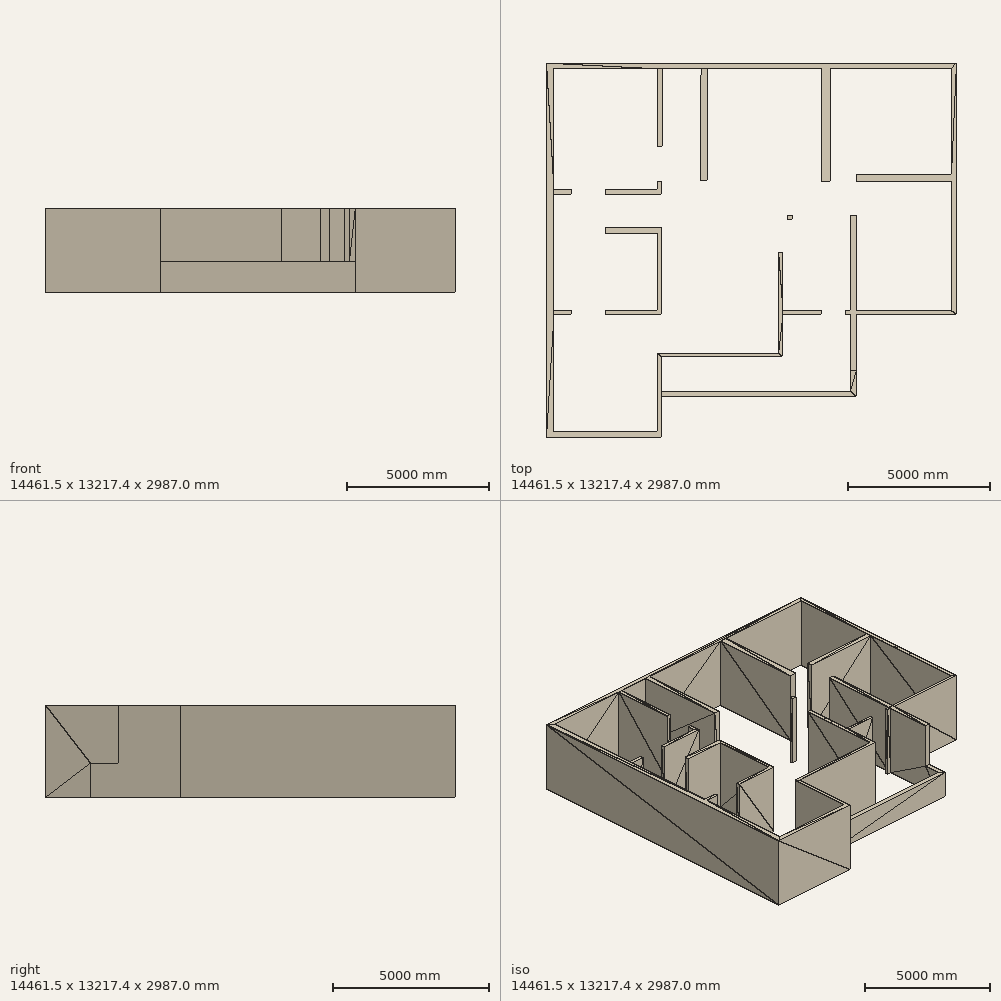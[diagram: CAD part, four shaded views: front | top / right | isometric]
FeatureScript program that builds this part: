
annotation { "Feature Type Name" : "Feature", "Feature Type Description" : "" }
export const myFeature = defineFeature(function(context is Context, id is Id, definition is map)
    precondition{}
    {
        {
            var Q0;
            Q0=qCreatedBy(makeId("Top.planeOp"),FACE);
            var sketch = newSketch(context, id + "F0", { "sketchPlane" : qUnion([Q0])});
            skLineSegment(sketch, "E0", {"start": v(0, 0) * mm, "end": v(-279.4, 0) * mm});
            skLineSegment(sketch, "E1", {"start": v(-863.6, -355.6) * mm, "end": v(-1168.4, -355.6) * mm});
            skLineSegment(sketch, "E2", {"start": v(-1168.4, -355.6) * mm, "end": v(-1168.4, -12.28) * mm});
            skLineSegment(sketch, "E3", {"start": v(-297.04, 0) * mm, "end": v(-311.21, 0) * mm});
            skLineSegment(sketch, "E4", {"start": v(0, 0) * mm, "end": v(0, 381) * mm});
            skLineSegment(sketch, "E5", {"start": v(-279.4, 381) * mm, "end": v(0, 381) * mm});
            skLineSegment(sketch, "E6", {"start": v(0, 399.22) * mm, "end": v(0, 711.2) * mm});
            skLineSegment(sketch, "E7", {"start": v(0, 711.2) * mm, "end": v(-355.6, 711.2) * mm});
            skLineSegment(sketch, "E8.bottom", {"start": v(-482.6, 279.4) * mm, "end": v(-467.2, 279.4) * mm});
            skLineSegment(sketch, "E8.top", {"start": v(-482.6, 268.26) * mm, "end": v(-467.2, 268.26) * mm});
            skLineSegment(sketch, "E8.left", {"start": v(-482.6, 279.4) * mm, "end": v(-482.6, 268.26) * mm});
            skLineSegment(sketch, "E8.right", {"start": v(-467.2, 279.4) * mm, "end": v(-467.2, 268.26) * mm});
            skLineSegment(sketch, "E9", {"start": v(-508, 0) * mm, "end": v(-508, -124.73) * mm});
            skLineSegment(sketch, "E10", {"start": v(-508, -124.73) * mm, "end": v(-863.6, -124.73) * mm});
            skLineSegment(sketch, "E11", {"start": v(-355.6, 381.3) * mm, "end": v(-355.6, 711.2) * mm});
            skLineSegment(sketch, "E12", {"start": v(-1168.4, 711.2) * mm, "end": v(-1168.4, 355.6) * mm});
            skLineSegment(sketch, "E13", {"start": v(-1168.4, 342.47) * mm, "end": v(-1168.4, 0) * mm});
            skLineSegment(sketch, "E14", {"start": v(-1168.4, 355.6) * mm, "end": v(-1117.6, 355.6) * mm});
            skLineSegment(sketch, "E15", {"start": v(-863.6, 355.6) * mm, "end": v(-863.6, 381) * mm});
            skLineSegment(sketch, "E16", {"start": v(-737.43, 382.75) * mm, "end": v(-736.18, 711.2) * mm});
            skLineSegment(sketch, "E17", {"start": v(-863.6, 711.2) * mm, "end": v(-863.6, 482.6) * mm});
            skLineSegment(sketch, "E18", {"start": v(-863.6, 0) * mm, "end": v(-863.6, 228.6) * mm});
            skLineSegment(sketch, "E19", {"start": v(-279.4, 0) * mm, "end": v(-279.4, 279.4) * mm});
            skLineSegment(sketch, "E20", {"start": v(-863.6, -355.6) * mm, "end": v(-863.6, -124.73) * mm});
            skLineSegment(sketch, "E21", {"start": v(-863.6, 0) * mm, "end": v(-1016, 0) * mm});
            skLineSegment(sketch, "E22", {"start": v(-1168.4, 0) * mm, "end": v(-1117.6, 0) * mm});
            skLineSegment(sketch, "E23", {"start": v(-863.6, 228.6) * mm, "end": v(-1016, 228.6) * mm});
            skLineSegment(sketch, "E24", {"start": v(-737.43, 382.75) * mm, "end": v(-716.3, 382.67) * mm});
            skLineSegment(sketch, "E25", {"start": v(-716.3, 382.67) * mm, "end": v(-716.3, 711.2) * mm});
            skLineSegment(sketch, "E26.trimOffspring", {"start": v(-736.18, 711.2) * mm, "end": v(-849.36, 711.2) * mm});
            skLineSegment(sketch, "E27", {"start": v(-849.36, 711.2) * mm, "end": v(-849.36, 482.6) * mm});
            skLineSegment(sketch, "E28", {"start": v(-849.36, 482.6) * mm, "end": v(-863.6, 482.6) * mm});
            skLineSegment(sketch, "E29.trimOffspring", {"start": v(-863.6, 711.2) * mm, "end": v(-1168.4, 711.2) * mm});
            skLineSegment(sketch, "E30", {"start": v(-1168.4, 342.47) * mm, "end": v(-1117.6, 342.47) * mm});
            skLineSegment(sketch, "E31", {"start": v(-852.49, 342.47) * mm, "end": v(-852.49, 381) * mm});
            skLineSegment(sketch, "E32", {"start": v(-852.49, 381) * mm, "end": v(-863.6, 381) * mm});
            skLineSegment(sketch, "E33", {"start": v(-1016, 228.6) * mm, "end": v(-1016, 244.83) * mm});
            skLineSegment(sketch, "E34", {"start": v(-1016, 244.83) * mm, "end": v(-852.49, 244.83) * mm});
            skLineSegment(sketch, "E35", {"start": v(-852.49, 244.83) * mm, "end": v(-852.49, -12.28) * mm});
            skLineSegment(sketch, "E36", {"start": v(-852.49, -12.28) * mm, "end": v(-1016, -12.28) * mm});
            skLineSegment(sketch, "E37", {"start": v(-1016, -12.28) * mm, "end": v(-1016, 0) * mm});
            skLineSegment(sketch, "E38", {"start": v(-1117.6, 0) * mm, "end": v(-1117.6, -12.28) * mm});
            skLineSegment(sketch, "E39", {"start": v(-1117.6, -12.28) * mm, "end": v(-1168.4, -12.28) * mm});
            skLineSegment(sketch, "E40", {"start": v(-279.4, 279.4) * mm, "end": v(-297.04, 279.4) * mm});
            skLineSegment(sketch, "E41", {"start": v(-297.04, 279.4) * mm, "end": v(-297.04, 0) * mm});
            skLineSegment(sketch, "E42", {"start": v(-279.4, 381) * mm, "end": v(-279.4, 399.44) * mm});
            skLineSegment(sketch, "E43", {"start": v(-279.4, 399.44) * mm, "end": v(0, 399.22) * mm});
            skLineSegment(sketch, "E44", {"start": v(-355.6, 381.3) * mm, "end": v(-380.93, 381.31) * mm});
            skLineSegment(sketch, "E45", {"start": v(-380.93, 381.31) * mm, "end": v(-380.93, 711.2) * mm});
            skLineSegment(sketch, "E46.trimOffspring", {"start": v(-380.93, 711.2) * mm, "end": v(-716.3, 711.2) * mm});
            skLineSegment(sketch, "E47", {"start": v(-1190.38, -355.6) * mm, "end": v(-1190.38, 727.92) * mm});
            skLineSegment(sketch, "E48", {"start": v(-1190.38, 727.92) * mm, "end": v(14.74, 727.92) * mm});
            skLineSegment(sketch, "E49", {"start": v(14.74, 727.92) * mm, "end": v(14.74, -10.6) * mm});
            skLineSegment(sketch, "E50", {"start": v(14.74, -10.6) * mm, "end": v(-279.4, -10.6) * mm});
            skLineSegment(sketch, "E51", {"start": v(-495.3, -10.6) * mm, "end": v(-495.3, -135.14) * mm});
            skLineSegment(sketch, "E52", {"start": v(-495.3, -135.14) * mm, "end": v(-852.25, -135.14) * mm});
            skLineSegment(sketch, "E53", {"start": v(-852.25, -135.14) * mm, "end": v(-852.25, -237.06) * mm});
            skLineSegment(sketch, "E54", {"start": v(-852.25, -373.53) * mm, "end": v(-1190.38, -373.53) * mm});
            skLineSegment(sketch, "E55", {"start": v(-1190.38, -373.53) * mm, "end": v(-1190.38, -355.6) * mm});
            skLineSegment(sketch, "E56", {"start": v(-311.21, 0) * mm, "end": v(-311.21, -10.6) * mm});
            skLineSegment(sketch, "E57", {"start": v(-382.22, 0) * mm, "end": v(-382.22, -10.6) * mm});
            skLineSegment(sketch, "E58.trimOffspring", {"start": v(-382.22, 0) * mm, "end": v(-495.3, 0) * mm});
            skLineSegment(sketch, "E59.trimOffspring", {"start": v(-382.22, -10.6) * mm, "end": v(-495.3, -10.6) * mm});
            skLineSegment(sketch, "E60", {"start": v(-279.4, -10.6) * mm, "end": v(-279.4, -252.35) * mm});
            skLineSegment(sketch, "E61", {"start": v(-279.4, -252.35) * mm, "end": v(-852.25, -252.35) * mm});
            skLineSegment(sketch, "E62", {"start": v(-297.04, -10.6) * mm, "end": v(-297.04, -237.06) * mm});
            skLineSegment(sketch, "E63", {"start": v(-297.04, -237.06) * mm, "end": v(-852.25, -237.06) * mm});
            skLineSegment(sketch, "E64.trimOffspring", {"start": v(-852.25, -252.35) * mm, "end": v(-852.25, -373.53) * mm});
            skLineSegment(sketch, "E65.trimOffspring", {"start": v(-297.04, -10.6) * mm, "end": v(-311.21, -10.6) * mm});
            skLineSegment(sketch, "E66", {"start": v(-1117.6, 342.47) * mm, "end": v(-1117.6, 355.6) * mm});
            skLineSegment(sketch, "E67", {"start": v(-1016, 342.47) * mm, "end": v(-1016, 355.6) * mm});
            skLineSegment(sketch, "E68.trimOffspring", {"start": v(-1016, 355.6) * mm, "end": v(-863.6, 355.6) * mm});
            skLineSegment(sketch, "E69.trimOffspring", {"start": v(-1016, 342.47) * mm, "end": v(-852.49, 342.47) * mm});
            skLineSegment(sketch, "E70", {"start": v(-508, 0) * mm, "end": v(-508, 170.24) * mm});
            skLineSegment(sketch, "E71", {"start": v(-508, 170.24) * mm, "end": v(-495.3, 170.24) * mm});
            skLineSegment(sketch, "E72", {"start": v(-495.3, 170.24) * mm, "end": v(-495.3, 0) * mm});
            skSolve(sketch);
        }
        {
            var Q0;
            Q0=makeQuery(id+"F0.imprint","IMPRINT",FACE,{"disambiguationData":[TD([[makeQuery(id+"F0.imprint","IMPRINT",EDGE,{"derivedFrom":sQuery(id+"F0.wireOp",EDGE,"E0")}),1.0]])]});
            var Q1;
            Q1=makeQuery(id+"F0.imprint","IMPRINT",FACE,{"disambiguationData":[TD([[makeQuery(id+"F0.imprint","IMPRINT",EDGE,{"derivedFrom":sQuery(id+"F0.wireOp",EDGE,"E18")}),-1.0]])]});
            var Q2;
            Q2=makeQuery(id+"F0.imprint","IMPRINT",FACE,{"disambiguationData":[TD([[makeQuery(id+"F0.imprint","IMPRINT",EDGE,{"derivedFrom":sQuery(id+"F0.wireOp",EDGE,"E8.bottom")}),-1.0]])]});
            var Q3;
            Q3=makeQuery(id+"F0.imprint","IMPRINT",FACE,{"disambiguationData":[TD([[makeQuery(id+"F0.imprint","IMPRINT",EDGE,{"derivedFrom":sQuery(id+"F0.wireOp",EDGE,"E15")}),-1.0]])]});
            extrude(context, id + "F1", {"entities" : qUnion([Q0, Q1, Q2, Q3]), "depth" : 248.92 * mm});
        }
        {
            var Q0;
            Q0=makeQuery(id+"F1.opExtrude","SWEPT_FACE",FACE,{"disambiguationData":[OSD([sQuery(id+"F0.wireOp",EDGE,"E61")])]});
            var sketch = newSketch(context, id + "F2", { "sketchPlane" : qUnion([Q0])});
            skLineSegment(sketch, "E73.bottom", {"start": v(-852.25, 248.92) * mm, "end": v(-279.4, 248.92) * mm});
            skLineSegment(sketch, "E73.top", {"start": v(-852.25, 92.8) * mm, "end": v(-279.4, 92.8) * mm});
            skLineSegment(sketch, "E73.left", {"start": v(-852.25, 248.92) * mm, "end": v(-852.25, 92.8) * mm});
            skLineSegment(sketch, "E73.right", {"start": v(-279.4, 248.92) * mm, "end": v(-279.4, 92.8) * mm});
            skSolve(sketch);
        }
        {
            var Q0;
            Q0=makeQuery(id+"F2.imprint","IMPRINT",FACE,{"disambiguationData":[TD([[makeQuery(id+"F2.imprint","IMPRINT",EDGE,{"derivedFrom":sQuery(id+"F2.wireOp",EDGE,"E73.bottom")}),1.0]])]});
            extrude(context, id + "F3", {"entities" : qUnion([Q0]), "operationType" : NewBodyOperationType.REMOVE, "oppositeDirection" : true, "depth" : 76.2 * mm});
        }
        {
            var Q0;
            Q0=makeQuery(id+"F1.opExtrude","SWEPT_BODY",BODY,{"disambiguationData":[OSD([sQuery(id+"F0.wireOp",EDGE,"E0"),sQuery(id+"F0.wireOp",EDGE,"E1"),sQuery(id+"F0.wireOp",EDGE,"E2"),sQuery(id+"F0.wireOp",EDGE,"E3"),sQuery(id+"F0.wireOp",EDGE,"E4"),sQuery(id+"F0.wireOp",EDGE,"E5"),sQuery(id+"F0.wireOp",EDGE,"E6"),sQuery(id+"F0.wireOp",EDGE,"E7"),sQuery(id+"F0.wireOp",EDGE,"E9"),sQuery(id+"F0.wireOp",EDGE,"E10"),sQuery(id+"F0.wireOp",EDGE,"E11"),sQuery(id+"F0.wireOp",EDGE,"E12"),sQuery(id+"F0.wireOp",EDGE,"E13"),sQuery(id+"F0.wireOp",EDGE,"E14"),sQuery(id+"F0.wireOp",EDGE,"E15"),sQuery(id+"F0.wireOp",EDGE,"E16"),sQuery(id+"F0.wireOp",EDGE,"E17"),sQuery(id+"F0.wireOp",EDGE,"E19"),sQuery(id+"F0.wireOp",EDGE,"E20"),sQuery(id+"F0.wireOp",EDGE,"E22"),sQuery(id+"F0.wireOp",EDGE,"E24"),sQuery(id+"F0.wireOp",EDGE,"E25"),sQuery(id+"F0.wireOp",EDGE,"E26.trimOffspring"),sQuery(id+"F0.wireOp",EDGE,"E27"),sQuery(id+"F0.wireOp",EDGE,"E28"),sQuery(id+"F0.wireOp",EDGE,"E29.trimOffspring"),sQuery(id+"F0.wireOp",EDGE,"E30"),sQuery(id+"F0.wireOp",EDGE,"E31"),sQuery(id+"F0.wireOp",EDGE,"E32"),sQuery(id+"F0.wireOp",EDGE,"E38"),sQuery(id+"F0.wireOp",EDGE,"E39"),sQuery(id+"F0.wireOp",EDGE,"E40"),sQuery(id+"F0.wireOp",EDGE,"E41"),sQuery(id+"F0.wireOp",EDGE,"E42"),sQuery(id+"F0.wireOp",EDGE,"E43"),sQuery(id+"F0.wireOp",EDGE,"E44"),sQuery(id+"F0.wireOp",EDGE,"E45"),sQuery(id+"F0.wireOp",EDGE,"E46.trimOffspring"),sQuery(id+"F0.wireOp",EDGE,"E47"),sQuery(id+"F0.wireOp",EDGE,"E48"),sQuery(id+"F0.wireOp",EDGE,"E49"),sQuery(id+"F0.wireOp",EDGE,"E50"),sQuery(id+"F0.wireOp",EDGE,"E51"),sQuery(id+"F0.wireOp",EDGE,"E52"),sQuery(id+"F0.wireOp",EDGE,"E53"),sQuery(id+"F0.wireOp",EDGE,"E54"),sQuery(id+"F0.wireOp",EDGE,"E55"),sQuery(id+"F0.wireOp",EDGE,"E56"),sQuery(id+"F0.wireOp",EDGE,"E57"),sQuery(id+"F0.wireOp",EDGE,"E58.trimOffspring"),sQuery(id+"F0.wireOp",EDGE,"E59.trimOffspring"),sQuery(id+"F0.wireOp",EDGE,"E60"),sQuery(id+"F0.wireOp",EDGE,"E61"),sQuery(id+"F0.wireOp",EDGE,"E62"),sQuery(id+"F0.wireOp",EDGE,"E63"),sQuery(id+"F0.wireOp",EDGE,"E64.trimOffspring"),sQuery(id+"F0.wireOp",EDGE,"E65.trimOffspring")])]});
            var Q1;
            Q1=makeQuery(id+"F1.opExtrude","SWEPT_BODY",BODY,{"disambiguationData":[OSD([sQuery(id+"F0.wireOp",EDGE,"E8.bottom"),sQuery(id+"F0.wireOp",EDGE,"E8.top"),sQuery(id+"F0.wireOp",EDGE,"E8.left"),sQuery(id+"F0.wireOp",EDGE,"E8.right")])]});
            var Q2;
            Q2=makeQuery(id+"F1.opExtrude","SWEPT_BODY",BODY,{"disambiguationData":[OSD([sQuery(id+"F0.wireOp",EDGE,"E18"),sQuery(id+"F0.wireOp",EDGE,"E21"),sQuery(id+"F0.wireOp",EDGE,"E23"),sQuery(id+"F0.wireOp",EDGE,"E33"),sQuery(id+"F0.wireOp",EDGE,"E34"),sQuery(id+"F0.wireOp",EDGE,"E35"),sQuery(id+"F0.wireOp",EDGE,"E36"),sQuery(id+"F0.wireOp",EDGE,"E37")])]});
            var Q3;
            Q3=makeQuery(id+"F1.opExtrude","SWEPT_BODY",BODY,{"disambiguationData":[OSD([sQuery(id+"F0.wireOp",EDGE,"E15"),sQuery(id+"F0.wireOp",EDGE,"E31"),sQuery(id+"F0.wireOp",EDGE,"E32"),sQuery(id+"F0.wireOp",EDGE,"E67"),sQuery(id+"F0.wireOp",EDGE,"E68.trimOffspring"),sQuery(id+"F0.wireOp",EDGE,"E69.trimOffspring")])]});
            var Q4;
            Q4=qCreatedBy(makeId("Origin.pointOp"),VERTEX);
            transform(context, id + "F4", {"entities" : qUnion([Q0, Q1, Q2, Q3]), "transformType" : TransformType.SCALE_UNIFORMLY, "scale" : 12, "scalePoint" : qUnion([Q4]), "makeCopy" : false});
        }
    });
